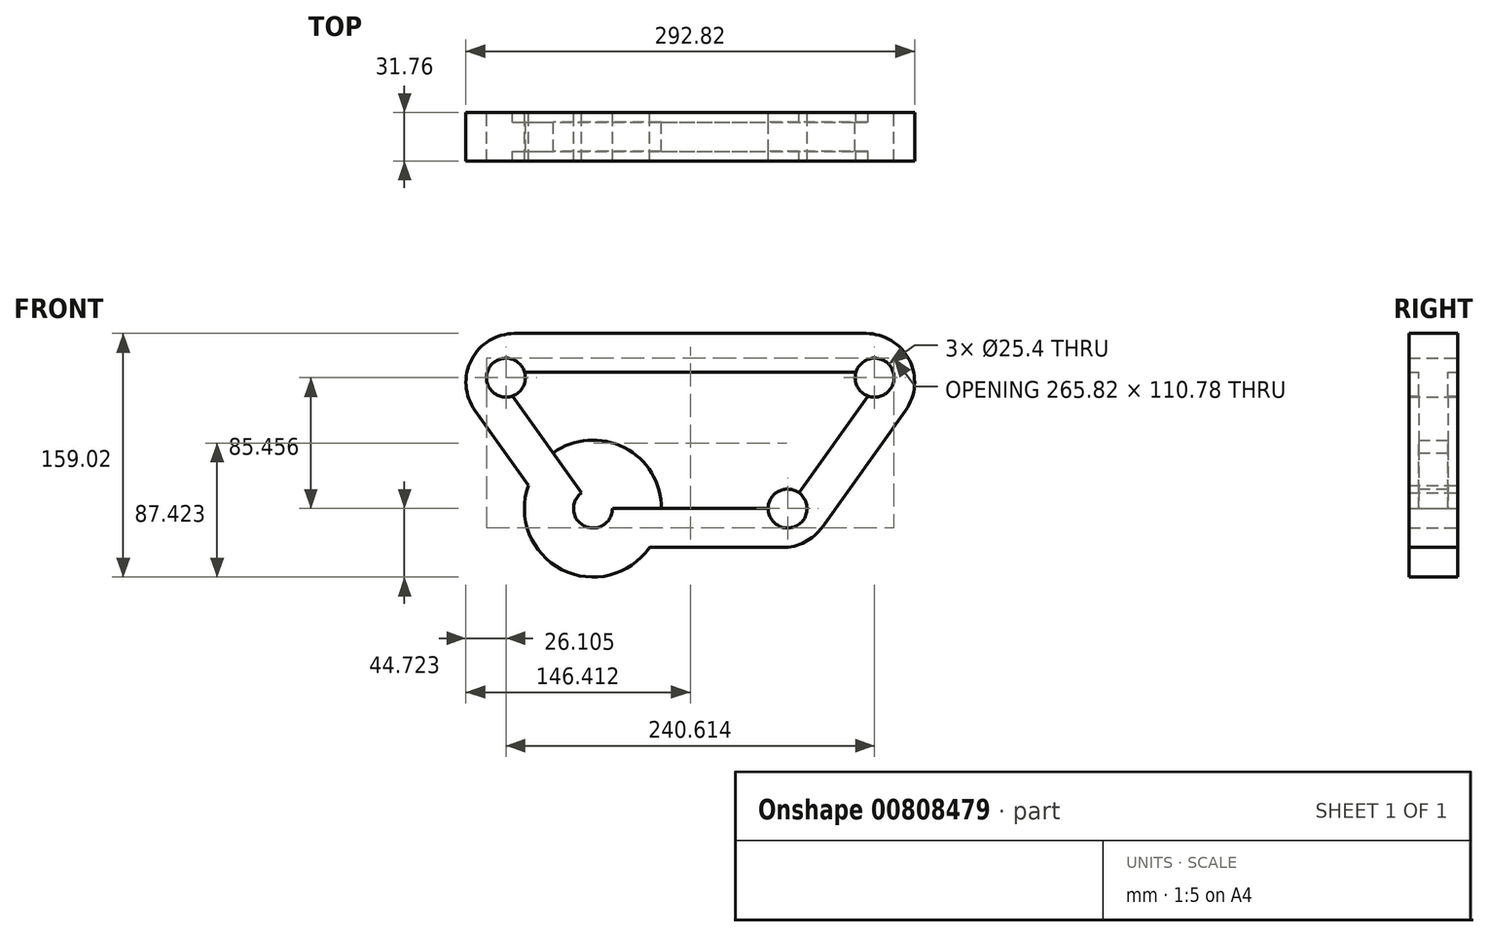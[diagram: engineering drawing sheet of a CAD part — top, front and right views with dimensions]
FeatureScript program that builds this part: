
annotation { "Feature Type Name" : "Feature", "Feature Type Description" : "" }
export const myFeature = defineFeature(function(context is Context, id is Id, definition is map)
    precondition{}
    {
        {
            var Q0;
            Q0=qCreatedBy(makeId("Front.planeOp"),FACE);
            var sketch = newSketch(context, id + "F0", { "sketchPlane" : qUnion([Q0])});
            skLineSegment(sketch, "E0", {"start": v(161.27, 39.63) * mm, "end": v(106.84, -36.57) * mm});
            skLineSegment(sketch, "E1", {"start": v(-78.39, 39.63) * mm, "end": v(-23.96, -36.57) * mm});
            skLineSegment(sketch, "E2", {"start": v(-18.8, -39.23) * mm, "end": v(101.67, -39.23) * mm});
            skLineSegment(sketch, "E3", {"start": v(-73.22, 49.67) * mm, "end": v(156.1, 49.67) * mm});
            skPoint(sketch, "E4.visualSharp", {"position": v(-85.56, 49.67) * mm});
            skArc(sketch, "E4.filletArc", {"start": v(-73.22, 49.67) * mm, "mid": v(-78.87, 46.23) * mm, "end": v(-78.39, 39.63) * mm});
            skPoint(sketch, "E5.visualSharp", {"position": v(168.44, 49.67) * mm});
            skArc(sketch, "E5.filletArc", {"start": v(161.27, 39.63) * mm, "mid": v(161.75, 46.23) * mm, "end": v(156.1, 49.67) * mm});
            skPoint(sketch, "E6.visualSharp", {"position": v(-22.06, -39.23) * mm});
            skArc(sketch, "E6.filletArc", {"start": v(-23.96, -36.57) * mm, "mid": v(-21.7, -38.52) * mm, "end": v(-18.8, -39.23) * mm});
            skPoint(sketch, "E7.visualSharp", {"position": v(104.94, -39.23) * mm});
            skArc(sketch, "E7.filletArc", {"start": v(101.67, -39.23) * mm, "mid": v(104.58, -38.52) * mm, "end": v(106.84, -36.57) * mm});
            skCircle(sketch, "E8", {"center": v(-78.87, 46.23) * mm, "radius": 12.7 * mm});
            skCircle(sketch, "E9", {"center": v(-22.06, -39.23) * mm, "radius": 12.7 * mm});
            skCircle(sketch, "E10", {"center": v(104.94, -39.23) * mm, "radius": 12.7 * mm});
            skCircle(sketch, "E11", {"center": v(161.75, 46.23) * mm, "radius": 12.7 * mm});
            skArc(sketch, "E12.0", {"start": v(-73.22, 75.07) * mm, "mid": v(-101.45, 57.85) * mm, "end": v(-99.06, 24.87) * mm});
            skLineSegment(sketch, "E12.1", {"start": v(-73.22, 75.07) * mm, "end": v(156.1, 75.07) * mm});
            skLineSegment(sketch, "E12.2", {"start": v(-99.06, 24.87) * mm, "end": v(-44.63, -51.33) * mm});
            skArc(sketch, "E12.3", {"start": v(181.94, 24.87) * mm, "mid": v(184.33, 57.85) * mm, "end": v(156.1, 75.07) * mm});
            skArc(sketch, "E12.4", {"start": v(-44.63, -51.33) * mm, "mid": v(-33.32, -61.1) * mm, "end": v(-18.8, -64.63) * mm});
            skLineSegment(sketch, "E12.5", {"start": v(-18.8, -64.63) * mm, "end": v(101.67, -64.63) * mm});
            skArc(sketch, "E12.6", {"start": v(101.67, -64.63) * mm, "mid": v(116.2, -61.1) * mm, "end": v(127.5, -51.33) * mm});
            skLineSegment(sketch, "E12.7", {"start": v(181.94, 24.87) * mm, "end": v(127.5, -51.33) * mm});
            skCircle(sketch, "E13", {"center": v(-22.06, -39.23) * mm, "radius": 44.72 * mm});
            skSolve(sketch);
        }
        {
            var Q0;
            Q0 = qSketchRegion(id + "F0", true);
            extrude(context, id + "F1", {"entities" : qUnion([Q0]), "endBound" : BoundingType.SYMMETRIC, "depth" : 31.75 * mm, "offsetDistance" : 25.4 * mm});
        }
        {
            var Q0;
            {var subQ3=sQuery(id+"F0.wireOp",EDGE,"E11");var subQ13=sQuery(id+"F0.wireOp",EDGE,"E0");var subQ14=makeQuery(id+"F0.imprint","INTERSECT",VERTEX,{"derivedFrom":[subQ13,subQ3]});Q0=makeQuery(id+"F0.imprint","IMPRINT",FACE,{"disambiguationData":[TD([[makeQuery(id+"F0.imprint","IMPRINT",EDGE,{"disambiguationData":[TD([[subQ14,-1.0]])],"derivedFrom":subQ13}),-1.0]])]});}
            extrude(context, id + "F2", {"entities" : qUnion([Q0]), "operationType" : NewBodyOperationType.ADD, "endBound" : BoundingType.SYMMETRIC, "depth" : 19.05 * mm, "offsetDistance" : 25.4 * mm});
        }
    });
